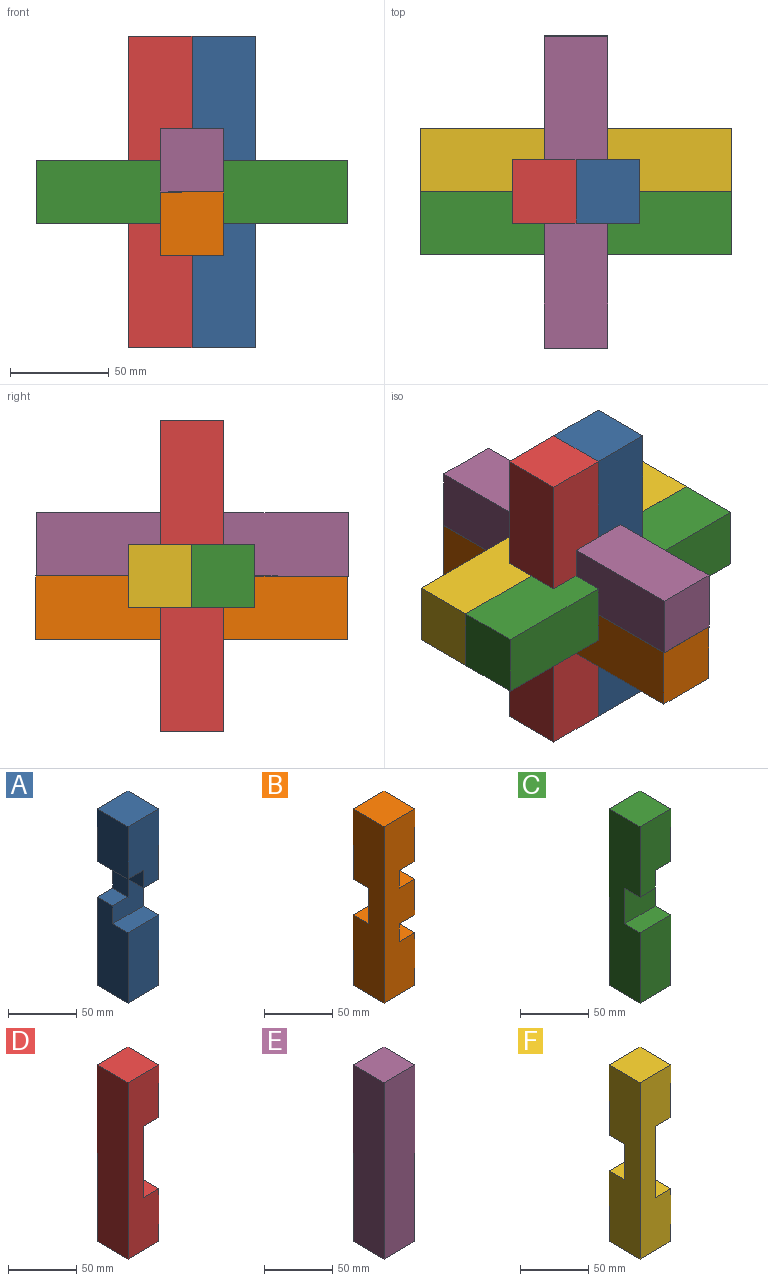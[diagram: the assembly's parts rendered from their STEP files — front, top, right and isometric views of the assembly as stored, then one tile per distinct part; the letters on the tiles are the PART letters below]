
ASSEMBLY  parts=6 mates=14
PART A: 14 faces, bbox 32x32x158 mm
  f0: plane 79x32mm, normal (-1,0,0), area 2272mm2, adj f3,f4,f6,f9,f10,f11
  f1: plane 63x32mm, normal (0,-1,0), area 1760mm2, adj f2,f5,f7,f8,f12,f13
  f2: plane 16x16mm, normal (0,0,-1), area 256mm2, adj f1,f3,f5,f13
  f3: plane 32x32mm, normal (0,-1,0), area 768mm2, adj f0,f2,f5,f10,f11,f13
  f4: plane 63x32mm, normal (0,-1,0), area 2016mm2, adj f0,f5,f9,f10
  f5: plane 158x32mm, normal (1,0,0), area 4544mm2, adj f1,f2,f3,f4,f6,f8,f9,f10
  f6: plane 158x32mm, normal (0,1,0), area 4544mm2, adj f0,f5,f7,f8,f9,f11,f12,f13
  f7: plane 47x32mm, normal (-1,0,0), area 1504mm2, adj f1,f6,f8,f12
  f8: plane 32x32mm, normal (0,0,1), area 1024mm2, adj f1,f5,f6,f7
  f9: plane 32x32mm, normal (0,0,-1), area 1024mm2, adj f0,f4,f5,f6
  f10: plane 32x16mm, normal (0,0,1), area 512mm2, adj f0,f3,f4,f5
  f11: plane 16x16mm, normal (0,0,1), area 256mm2, adj f0,f3,f6,f13
  f12: plane 32x16mm, normal (0,0,-1), area 512mm2, adj f1,f6,f7,f13
  f13: plane 32x32mm, normal (-1,0,0), area 768mm2, adj f1,f2,f3,f6,f11,f12
PART B: 18 faces, bbox 32x32x158 mm
  f0: plane 32x16mm, normal (1,0,0), area 512mm2, adj f4,f6,f11,f13,f16
  f1: plane 63x32mm, normal (0,1,0), area 1760mm2, adj f2,f5,f7,f8,f10,f12
  f2: plane 32x16mm, normal (1,0,0), area 512mm2, adj f1,f4,f10,f12,f15
  f3: plane 47x32mm, normal (1,0,0), area 1504mm2, adj f4,f6,f9,f11
  f4: plane 158x32mm, normal (0,-1,0), area 4544mm2, adj f0,f2,f3,f5,f7,f8,f9,f10
  f5: plane 47x32mm, normal (1,0,0), area 1504mm2, adj f1,f4,f8,f10
  f6: plane 63x32mm, normal (0,1,0), area 1760mm2, adj f0,f3,f7,f9,f11,f13
  f7: plane 158x32mm, normal (-1,0,0), area 4544mm2, adj f1,f4,f6,f8,f9,f12,f13,f14
  f8: plane 32x32mm, normal (0,0,1), area 1024mm2, adj f1,f4,f5,f7
  f9: plane 32x32mm, normal (0,0,-1), area 1024mm2, adj f3,f4,f6,f7
  f10: plane 32x16mm, normal (0,0,-1), area 512mm2, adj f1,f2,f4,f5
  f11: plane 32x16mm, normal (0,0,1), area 512mm2, adj f0,f3,f4,f6
  f12: plane 16x16mm, normal (0,0,-1), area 256mm2, adj f1,f2,f7,f14
  f13: plane 16x16mm, normal (0,0,1), area 256mm2, adj f0,f6,f7,f14
  f14: plane 32x32mm, normal (0,1,0), area 1024mm2, adj f7,f12,f13,f15,f16,f17
  f15: plane 16x16mm, normal (0,0,1), area 256mm2, adj f2,f4,f14,f17
  f16: plane 16x16mm, normal (0,0,-1), area 256mm2, adj f0,f4,f14,f17
  f17: plane 32x16mm, normal (1,0,0), area 512mm2, adj f4,f14,f15,f16
PART C: 14 faces, bbox 32x32x158 mm
  f0: plane 79x32mm, normal (1,0,0), area 2272mm2, adj f3,f5,f8,f9,f10,f11
  f1: plane 63x32mm, normal (0,-1,0), area 1760mm2, adj f2,f4,f6,f7,f12,f13
  f2: plane 16x16mm, normal (0,0,-1), area 256mm2, adj f1,f6,f10,f13
  f3: plane 63x32mm, normal (0,-1,0), area 2016mm2, adj f0,f6,f8,f9
  f4: plane 47x32mm, normal (1,0,0), area 1504mm2, adj f1,f5,f7,f12
  f5: plane 158x32mm, normal (0,1,0), area 4544mm2, adj f0,f4,f6,f7,f8,f11,f12,f13
  f6: plane 158x32mm, normal (-1,0,0), area 4544mm2, adj f1,f2,f3,f5,f7,f8,f9,f10
  f7: plane 32x32mm, normal (0,0,1), area 1024mm2, adj f1,f4,f5,f6
  f8: plane 32x32mm, normal (0,0,-1), area 1024mm2, adj f0,f3,f5,f6
  f9: plane 32x16mm, normal (0,0,1), area 512mm2, adj f0,f3,f6,f10
  f10: plane 32x32mm, normal (0,-1,0), area 768mm2, adj f0,f2,f6,f9,f11,f13
  f11: plane 16x16mm, normal (0,0,1), area 256mm2, adj f0,f5,f10,f13
  f12: plane 32x16mm, normal (0,0,-1), area 512mm2, adj f1,f4,f5,f13
  f13: plane 32x32mm, normal (1,0,0), area 768mm2, adj f1,f2,f5,f10,f11,f12
PART D: 10 faces, bbox 32x32x158 mm
  f0: plane 47x32mm, normal (1,0,0), area 1504mm2, adj f1,f3,f6,f8
  f1: plane 158x32mm, normal (0,-1,0), area 4032mm2, adj f0,f2,f4,f5,f6,f7,f8,f9
  f2: plane 47x32mm, normal (1,0,0), area 1504mm2, adj f1,f3,f5,f7
  f3: plane 158x32mm, normal (0,1,0), area 4032mm2, adj f0,f2,f4,f5,f6,f7,f8,f9
  f4: plane 158x32mm, normal (-1,0,0), area 5056mm2, adj f1,f3,f5,f6
  f5: plane 32x32mm, normal (0,0,1), area 1024mm2, adj f1,f2,f3,f4
  f6: plane 32x32mm, normal (0,0,-1), area 1024mm2, adj f0,f1,f3,f4
  f7: plane 32x16mm, normal (0,0,-1), area 512mm2, adj f1,f2,f3,f9
  f8: plane 32x16mm, normal (0,0,1), area 512mm2, adj f0,f1,f3,f9
  f9: plane 64x32mm, normal (1,0,0), area 2048mm2, adj f1,f3,f7,f8
PART E: 6 faces, bbox 32x32x158 mm
  f0: plane 158x32mm, normal (1,0,0), area 5056mm2, adj f1,f3,f4,f5
  f1: plane 158x32mm, normal (0,1,0), area 5056mm2, adj f0,f2,f4,f5
  f2: plane 158x32mm, normal (-1,0,0), area 5056mm2, adj f1,f3,f4,f5
  f3: plane 158x32mm, normal (0,-1,0), area 5056mm2, adj f0,f2,f4,f5
  f4: plane 32x32mm, normal (0,0,1), area 1024mm2, adj f0,f1,f2,f3
  f5: plane 32x32mm, normal (0,0,-1), area 1024mm2, adj f0,f1,f2,f3
PART F: 14 faces, bbox 32x32x158 mm
  f0: plane 63x32mm, normal (0,1,0), area 1760mm2, adj f1,f4,f6,f7,f9,f11
  f1: plane 64x32mm, normal (1,0,0), area 1536mm2, adj f0,f3,f5,f9,f10,f11,f12,f13
  f2: plane 47x32mm, normal (1,0,0), area 1504mm2, adj f3,f5,f8,f10
  f3: plane 158x32mm, normal (0,-1,0), area 4032mm2, adj f1,f2,f4,f6,f7,f8,f9,f10
  f4: plane 47x32mm, normal (1,0,0), area 1504mm2, adj f0,f3,f7,f9
  f5: plane 63x32mm, normal (0,1,0), area 1760mm2, adj f1,f2,f6,f8,f10,f12
  f6: plane 158x32mm, normal (-1,0,0), area 4544mm2, adj f0,f3,f5,f7,f8,f11,f12,f13
  f7: plane 32x32mm, normal (0,0,1), area 1024mm2, adj f0,f3,f4,f6
  f8: plane 32x32mm, normal (0,0,-1), area 1024mm2, adj f2,f3,f5,f6
  f9: plane 32x16mm, normal (0,0,-1), area 512mm2, adj f0,f1,f3,f4
  f10: plane 32x16mm, normal (0,0,1), area 512mm2, adj f1,f2,f3,f5
  f11: plane 16x16mm, normal (0,0,-1), area 256mm2, adj f0,f1,f6,f13
  f12: plane 16x16mm, normal (0,0,1), area 256mm2, adj f1,f5,f6,f13
  f13: plane 32x16mm, normal (0,1,0), area 512mm2, adj f1,f6,f11,f12
PLACE A t=(16.35,-6.85,-84.09)mm
PLACE B rot(axis=(-0.58,-0.58,-0.58),120deg) t=(0.35,-85.85,-21.09)mm fixed
PLACE C rot(axis=(-0.58,-0.58,0.58),120deg) t=(79.35,-22.85,-5.09)mm
PLACE D rot(axis=(0.03,-0.98,0.17),0deg) t=(-15.65,-6.85,-84.09)mm
PLACE E rot(axis=(1,0,0),90deg) t=(0.35,71.85,10.91)mm
PLACE F rot(axis=(0.58,-0.58,-0.58),120deg) t=(79.35,9.15,-5.09)mm
MATE planar A.f2 <-> C.f3  axis (0,0,-1) through (24.35,-14.85,10.91)mm
MATE planar F.f6 <-> B.f10  axis (0,1,0) through (0.35,25.15,-5.99)mm
MATE planar B.f4 <-> D.f9  axis (-1,0,0) through (-15.65,-6.85,-21.99)mm
MATE planar E.f2 <-> D.f9  axis (-1,0,0) through (-15.65,-7.15,10.91)mm
MATE planar F.f10 <-> A.f5  axis (-1,0,0) through (32.35,1.15,-5.09)mm
MATE planar C.f0 <-> A.f3  axis (0,1,0) through (43.4,-6.85,-5.99)mm
MATE planar B.f11 <-> C.f6  axis (0,1,0) through (0.35,-38.85,-13.09)mm
MATE planar E.f3 <-> B.f5  axis (0,0,-1) through (0.35,-7.15,-5.09)mm
MATE planar B.f14 <-> C.f11  axis (1,0,0) through (0.35,-6.85,-21.09)mm
MATE planar B.f14 <-> A.f0  axis (1,0,0) through (0.35,-6.85,-21.09)mm
MATE planar B.f0 <-> C.f5  axis (0,0,1) through (0.35,-30.85,-21.09)mm
MATE planar D.f1 <-> C.f13  axis (0,-1,0) through (-17.68,-22.85,-5.09)mm
MATE planar F.f3 <-> B.f2  axis (0,0,-1) through (0.35,11.19,-21.09)mm
MATE planar B.f7 <-> D.f8  axis (0,0,-1) through (-0.55,-6.85,-37.09)mm
